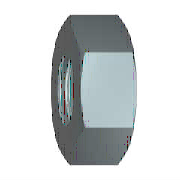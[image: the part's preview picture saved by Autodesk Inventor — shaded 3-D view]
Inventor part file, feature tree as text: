
AUTODESK INVENTOR PART (.ipt)
format: ipt  version: 2023 (Build 270158000, 158)  size: 164,864 bytes
history: native  units: mm (DEFAULTED — no unit token found)
features: sketch x3, other x2, extrude x1, hole x1, plane x1
ambient origin geometry x7: Origin, YZ Plane, XZ Plane, X Axis, Y Axis, Z Axis, Center Point
bodies: Solid1 (feature_tree)
feature tree (8):
  extrude  "Базовый элемент"  Depth=24.248711mm
  other  "Фаска1"
  hole  "Резьба"  [1 undecoded]
  other  "Work Axis1"
  plane  "Work Plane1"
  sketch  "Эскиз1"
  sketch  "Эскиз2"
  sketch  "Эскиз3"
note: 1 required parameter value undecoded (feature->parameter linkage not recoverable at this tier; creation-order binding heuristic only, values carry confidence <= 0.55)
